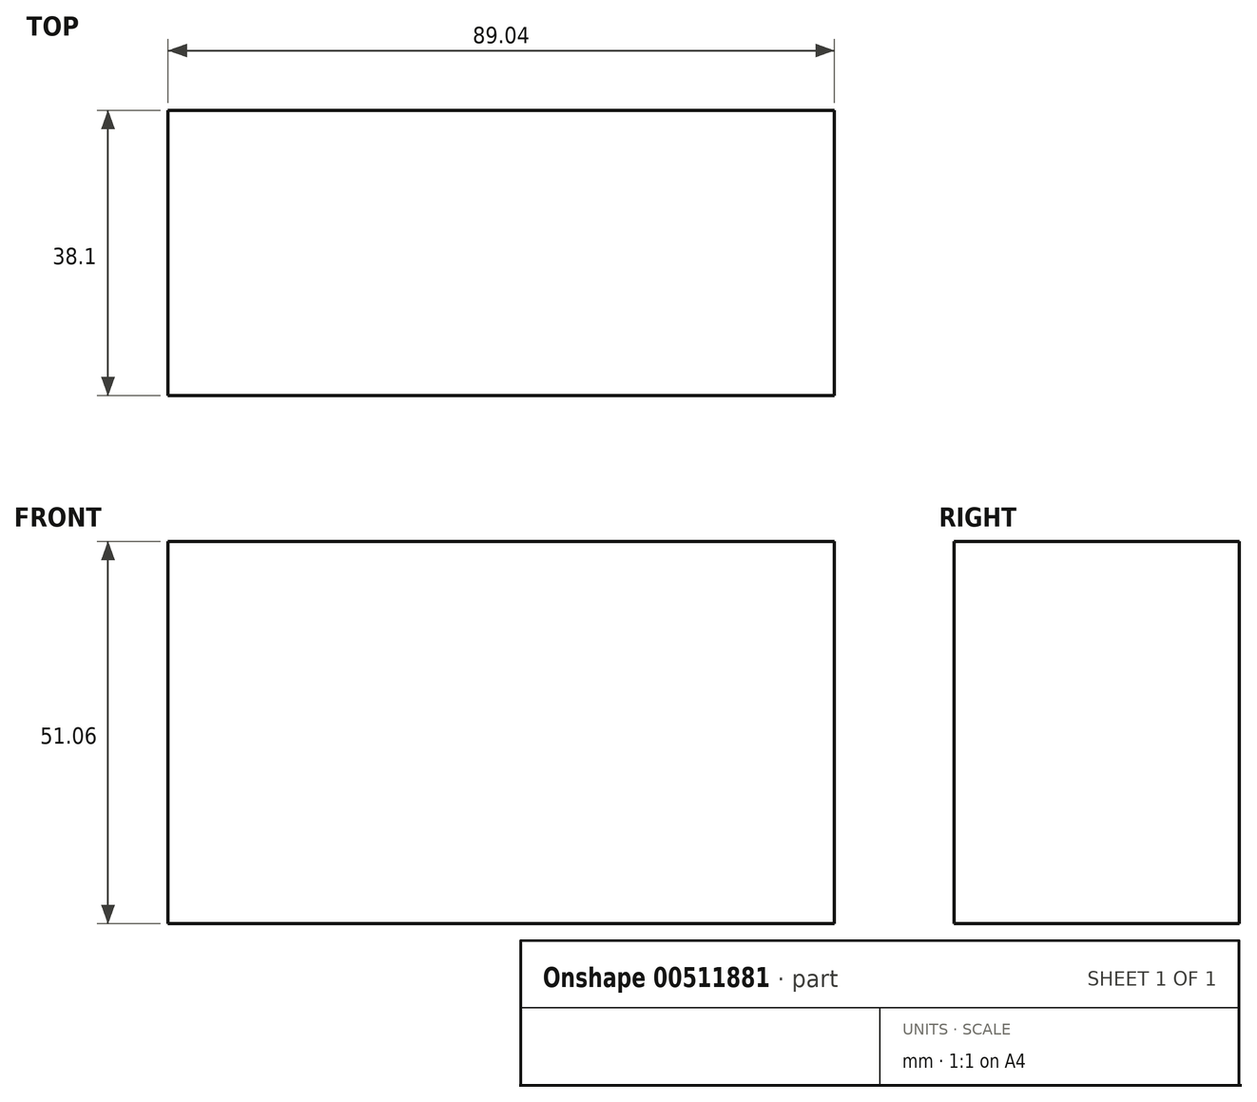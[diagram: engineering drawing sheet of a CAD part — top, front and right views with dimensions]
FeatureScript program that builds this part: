
annotation { "Feature Type Name" : "Feature", "Feature Type Description" : "" }
export const myFeature = defineFeature(function(context is Context, id is Id, definition is map)
    precondition{}
    {
        {
            var Q0;
            Q0=qCreatedBy(makeId("Front.planeOp"),FACE);
            var sketch = newSketch(context, id + "F0", { "sketchPlane" : qUnion([Q0])});
            skLineSegment(sketch, "E0", {"start": v(-36.27, 19) * mm, "end": v(52.77, 19) * mm});
            skLineSegment(sketch, "E1", {"start": v(52.77, 19) * mm, "end": v(52.77, -32.07) * mm});
            skLineSegment(sketch, "E2", {"start": v(-36.27, 19) * mm, "end": v(-36.27, -32.07) * mm});
            skLineSegment(sketch, "E3", {"start": v(-36.27, -32.07) * mm, "end": v(52.77, -32.07) * mm});
            skSolve(sketch);
        }
        {
            var Q0;
            Q0 = qSketchRegion(id + "F0", true);
            extrude(context, id + "F1", {"entities" : qUnion([Q0]), "depth" : 38.1 * mm});
        }
    });
